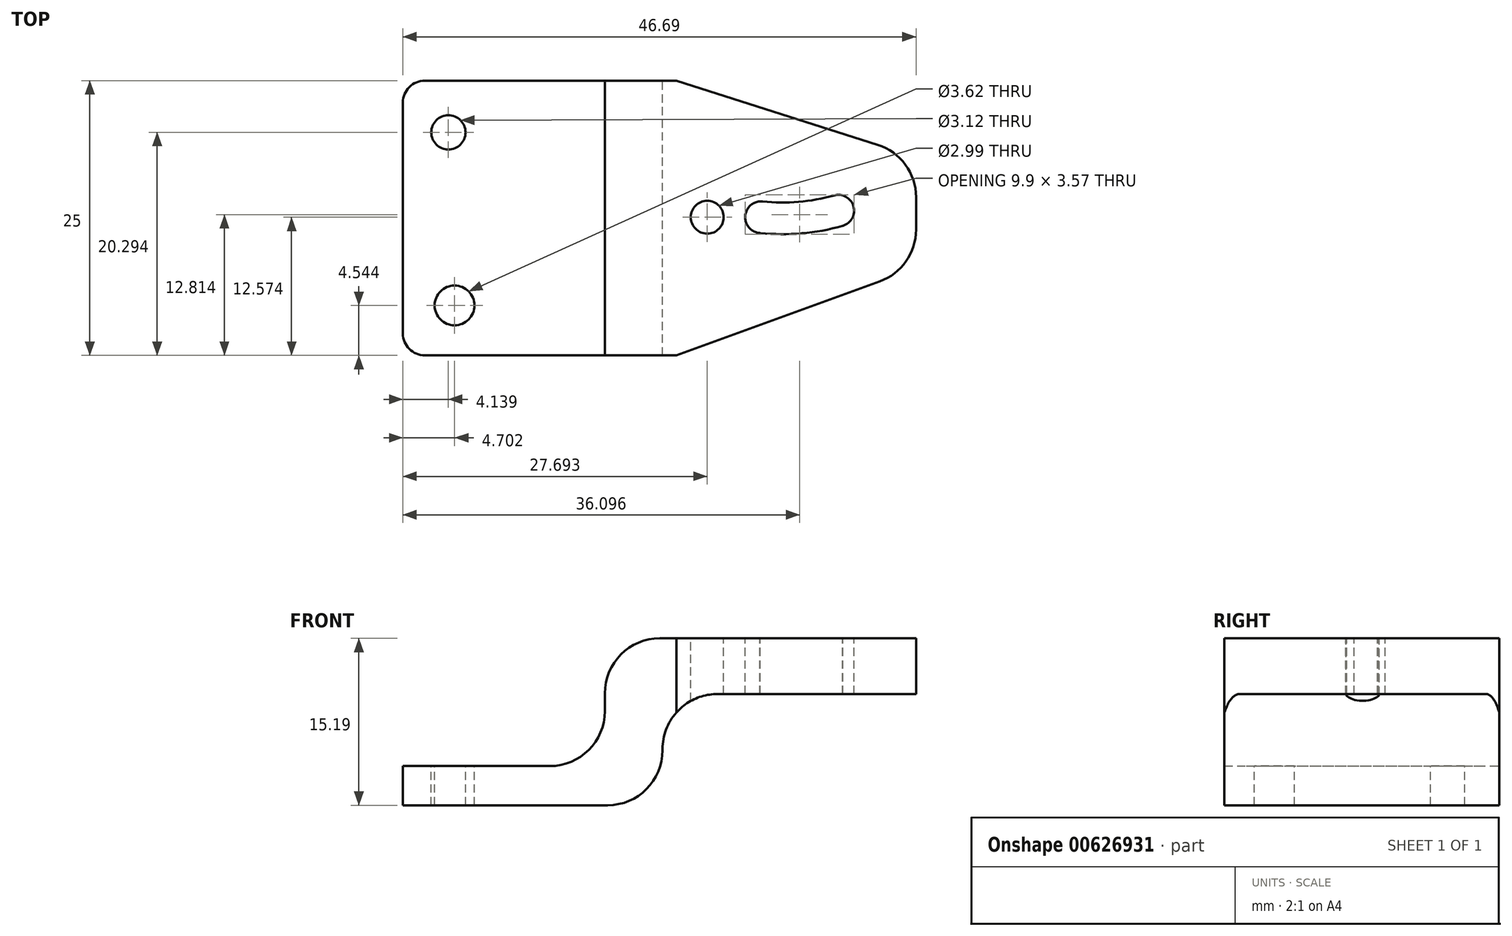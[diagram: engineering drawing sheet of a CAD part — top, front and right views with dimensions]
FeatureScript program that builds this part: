
annotation { "Feature Type Name" : "Feature", "Feature Type Description" : "" }
export const myFeature = defineFeature(function(context is Context, id is Id, definition is map)
    precondition{}
    {
        {
            var Q0;
            Q0=qCreatedBy(makeId("Front.planeOp"),FACE);
            var sketch = newSketch(context, id + "F0", { "sketchPlane" : qUnion([Q0])});
            skLineSegment(sketch, "E0", {"start": v(-43.78, -6.28) * mm, "end": v(-25.16, -6.28) * mm});
            skLineSegment(sketch, "E1", {"start": v(-20.16, -1.28) * mm, "end": v(-20.16, -1.16) * mm});
            skLineSegment(sketch, "E2", {"start": v(-15.16, 3.84) * mm, "end": v(2.9, 3.84) * mm});
            skLineSegment(sketch, "E3", {"start": v(2.9, 3.84) * mm, "end": v(2.9, 8.9) * mm});
            skLineSegment(sketch, "E4", {"start": v(2.9, 8.9) * mm, "end": v(-20.4, 8.9) * mm});
            skLineSegment(sketch, "E5", {"start": v(-25.4, 3.9) * mm, "end": v(-25.4, 2.28) * mm});
            skLineSegment(sketch, "E6", {"start": v(-30.4, -2.72) * mm, "end": v(-43.78, -2.72) * mm});
            skLineSegment(sketch, "E7", {"start": v(-43.78, -2.72) * mm, "end": v(-43.78, -6.28) * mm});
            skPoint(sketch, "E8.visualSharp", {"position": v(-25.4, 8.9) * mm});
            skArc(sketch, "E8.filletArc", {"start": v(-20.4, 8.9) * mm, "mid": v(-23.94, 7.44) * mm, "end": v(-25.4, 3.9) * mm});
            skPoint(sketch, "E9.visualSharp", {"position": v(-20.16, 3.84) * mm});
            skArc(sketch, "E9.filletArc", {"start": v(-15.16, 3.84) * mm, "mid": v(-18.7, 2.38) * mm, "end": v(-20.16, -1.16) * mm});
            skPoint(sketch, "E10.visualSharp", {"position": v(-25.4, -2.72) * mm});
            skArc(sketch, "E10.filletArc", {"start": v(-30.4, -2.72) * mm, "mid": v(-26.87, -1.25) * mm, "end": v(-25.4, 2.28) * mm});
            skPoint(sketch, "E11.visualSharp", {"position": v(-20.16, -6.28) * mm});
            skArc(sketch, "E11.filletArc", {"start": v(-25.16, -6.28) * mm, "mid": v(-21.62, -4.82) * mm, "end": v(-20.16, -1.28) * mm});
            skSolve(sketch);
        }
        {
            var Q0;
            Q0=makeQuery(id+"F0.imprint","IMPRINT",FACE,{"disambiguationData":[TD([[makeQuery(id+"F0.imprint","IMPRINT",EDGE,{"derivedFrom":sQuery(id+"F0.wireOp",EDGE,"E0")}),1.0]])]});
            extrude(context, id + "F1", {"entities" : qUnion([Q0]), "depth" : 25 * mm, "offsetDistance" : 25 * mm});
        }
        {
            var Q0;
            Q0=makeQuery(id+"F1.opExtrude","SWEPT_FACE",FACE,{"disambiguationData":[OSD([sQuery(id+"F0.wireOp",EDGE,"E6")])]});
            var sketch = newSketch(context, id + "F2", { "sketchPlane" : qUnion([Q0])});
            skCircle(sketch, "E12", {"center": v(-39.64, -4.7) * mm, "radius": 1.56 * mm});
            skCircle(sketch, "E13", {"center": v(-39.08, -20.46) * mm, "radius": 1.81 * mm});
            skSolve(sketch);
        }
        {
            var Q0;
            Q0=makeQuery(id+"F2.imprint","IMPRINT",FACE,{"disambiguationData":[TD([[makeQuery(id+"F2.imprint","IMPRINT",EDGE,{"derivedFrom":sQuery(id+"F2.wireOp",EDGE,"E12")}),1.0]])]});
            var Q1;
            Q1=makeQuery(id+"F2.imprint","IMPRINT",FACE,{"disambiguationData":[TD([[makeQuery(id+"F2.imprint","IMPRINT",EDGE,{"derivedFrom":sQuery(id+"F2.wireOp",EDGE,"E13")}),1.0]])]});
            extrude(context, id + "F3", {"entities" : qUnion([Q0, Q1]), "operationType" : NewBodyOperationType.REMOVE, "oppositeDirection" : true, "depth" : 25 * mm, "offsetDistance" : 25 * mm});
        }
        {
            var Q0;
            Q0=makeQuery(id+"F1.opExtrude","SWEPT_FACE",FACE,{"disambiguationData":[OSD([sQuery(id+"F0.wireOp",EDGE,"E4")])]});
            var sketch = newSketch(context, id + "F4", { "sketchPlane" : qUnion([Q0])});
            skCircle(sketch, "E14", {"center": v(-16.09, -12.43) * mm, "radius": 1.5 * mm});
            skArc(sketch, "E15", {"start": v(-11.05, -11) * mm, "mid": v(-7.78, -11.03) * mm, "end": v(-4.56, -10.45) * mm});
            skArc(sketch, "E16.0", {"start": v(-11.28, -13.87) * mm, "mid": v(-7.5, -13.9) * mm, "end": v(-3.77, -13.22) * mm});
            skArc(sketch, "E17", {"start": v(-11.05, -11) * mm, "mid": v(-12.63, -12.3) * mm, "end": v(-11.3, -13.86) * mm});
            skArc(sketch, "E18", {"start": v(-3.75, -13.2) * mm, "mid": v(-2.78, -11.43) * mm, "end": v(-4.56, -10.45) * mm});
            skLineSegment(sketch, "E19", {"start": v(2.9, -10.6) * mm, "end": v(2.9, -13.57) * mm});
            skLineSegment(sketch, "E20", {"start": v(-20.4, 0) * mm, "end": v(-20.4, -25) * mm});
            skLineSegment(sketch, "E21.0", {"start": v(-18.9, 0) * mm, "end": v(-18.9, -25) * mm});
            skLineSegment(sketch, "E22", {"start": v(-18.9, -25) * mm, "end": v(-0.39, -18.27) * mm});
            skLineSegment(sketch, "E23", {"start": v(-0.58, -5.83) * mm, "end": v(-18.9, 0) * mm});
            skPoint(sketch, "E24.visualSharp", {"position": v(2.9, -17.07) * mm});
            skArc(sketch, "E24.filletArc", {"start": v(-0.39, -18.27) * mm, "mid": v(2, -16.44) * mm, "end": v(2.9, -13.57) * mm});
            skPoint(sketch, "E25.newPointA", {"position": v(2.9, -7.07) * mm});
            skPoint(sketch, "E25.newPointB", {"position": v(3.31, -7.07) * mm});
            skArc(sketch, "E25.filletArc", {"start": v(2.9, -10.6) * mm, "mid": v(1.94, -7.65) * mm, "end": v(-0.58, -5.83) * mm});
            skLineSegment(sketch, "E26", {"start": v(-3.77, -13.22) * mm, "end": v(-3.75, -13.2) * mm});
            skLineSegment(sketch, "E27", {"start": v(-11.3, -13.86) * mm, "end": v(-11.28, -13.87) * mm});
            skSolve(sketch);
        }
        {
            var Q0;
            {var subQ0=sQuery(id+"F4.wireOp",EDGE,"E23");Q0=makeQuery(id+"F4.imprint","IMPRINT",FACE,{"disambiguationData":[TD([[makeQuery(id+"F4.imprint","IMPRINT",EDGE,{"derivedFrom":subQ0}),-1.0]])]});}
            var Q1;
            {var subQ0=sQuery(id+"F4.wireOp",EDGE,"E22");Q1=makeQuery(id+"F4.imprint","IMPRINT",FACE,{"disambiguationData":[TD([[makeQuery(id+"F4.imprint","IMPRINT",EDGE,{"derivedFrom":subQ0}),-1.0]])]});}
            var Q2;
            Q2=makeQuery(id+"F4.imprint","IMPRINT",FACE,{"disambiguationData":[TD([[makeQuery(id+"F4.imprint","IMPRINT",EDGE,{"derivedFrom":sQuery(id+"F4.wireOp",EDGE,"E14")}),1.0]])]});
            var Q3;
            Q3=makeQuery(id+"F4.imprint","IMPRINT",FACE,{"disambiguationData":[TD([[makeQuery(id+"F4.imprint","IMPRINT",EDGE,{"derivedFrom":sQuery(id+"F4.wireOp",EDGE,"E15")}),-1.0]])]});
            extrude(context, id + "F5", {"entities" : qUnion([Q0, Q1, Q2, Q3]), "operationType" : NewBodyOperationType.REMOVE, "oppositeDirection" : true, "depth" : 25 * mm, "offsetDistance" : 25 * mm});
        }
        {
            var Q0;
            Q0=makeQuery(id+"F1.opExtrude","CAP_EDGE",EDGE,{"disambiguationData":[OSD([sQuery(id+"F0.wireOp",EDGE,"E7")])],"isStart":true});
            var Q1;
            Q1=makeQuery(id+"F1.opExtrude","CAP_EDGE",EDGE,{"disambiguationData":[OSD([sQuery(id+"F0.wireOp",EDGE,"E7")])],"isStart":false});
            fillet(context, id + "F6", {"entities" : qUnion([Q0, Q1]), "radius" : 2 * mm, "tangentPropagation" : true, "allowEdgeOverflow" : false});
        }
    });
